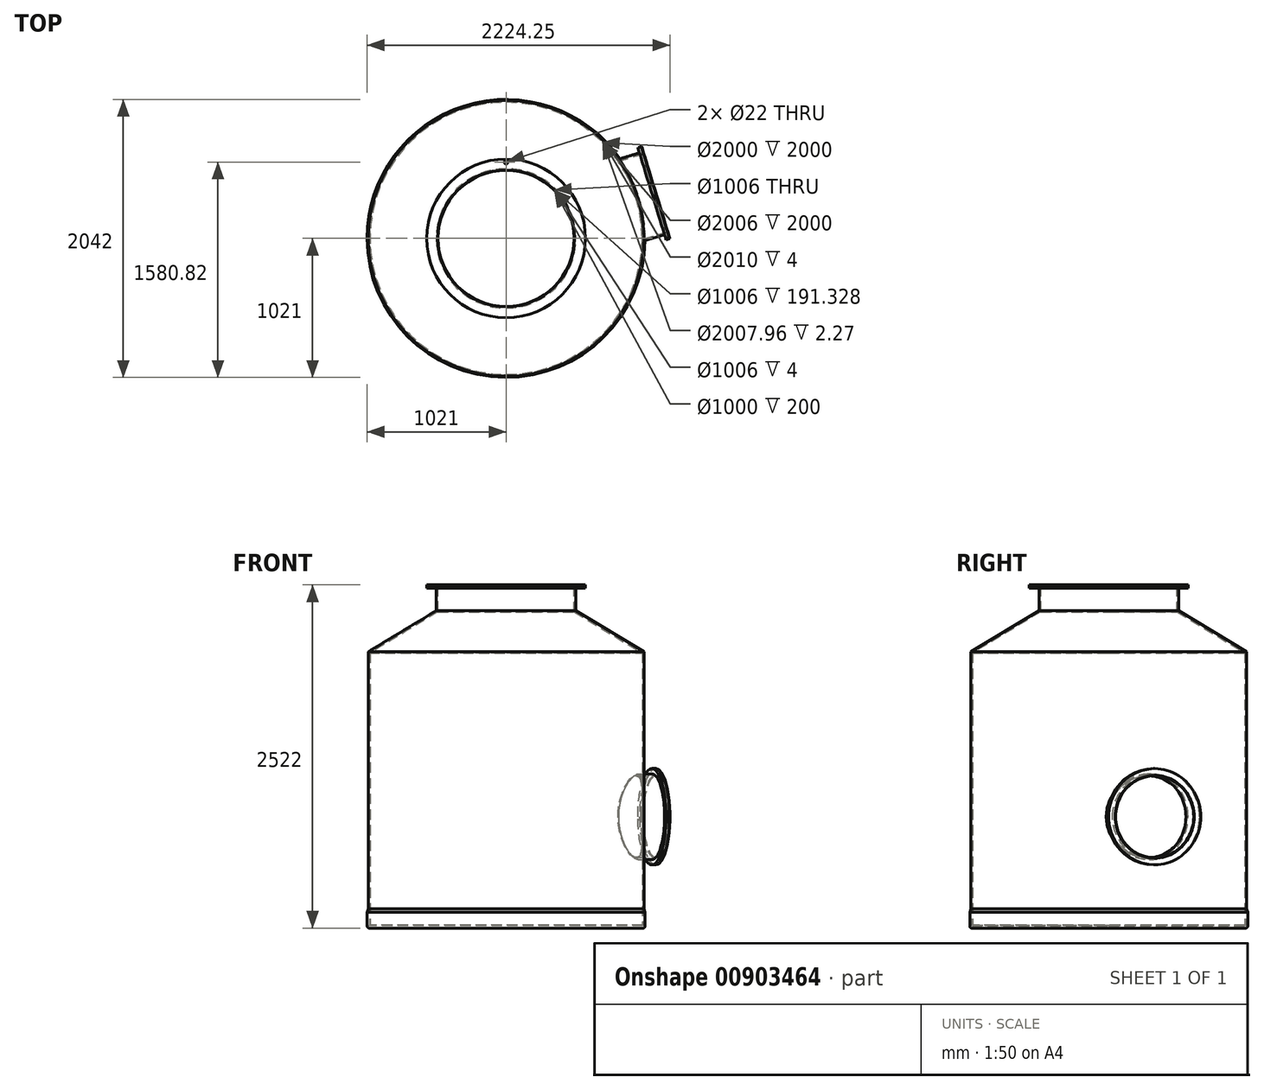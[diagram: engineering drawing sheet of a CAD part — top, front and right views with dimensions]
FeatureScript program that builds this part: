
annotation { "Feature Type Name" : "Feature", "Feature Type Description" : "" }
export const myFeature = defineFeature(function(context is Context, id is Id, definition is map)
    precondition{}
    {
        {
            var Q0;
            Q0=qCreatedBy(makeId("Top.planeOp"),FACE);
            var sketch = newSketch(context, id + "F0", { "sketchPlane" : qUnion([Q0])});
            skCircle(sketch, "E0", {"center": v(0, 0) * mm, "radius": 1005 * mm});
            skSolve(sketch);
        }
        {
            var Q0;
            Q0 = qSketchRegion(id + "F0", true);
            extrude(context, id + "F1", {"entities" : qUnion([Q0]), "depth" : 4 * mm, "offsetDistance" : 25 * mm});
        }
        {
            var Q0;
            Q0=makeQuery(id+"F1.opExtrude","CAP_FACE",FACE,{"disambiguationData":[OSD([sQuery(id+"F0.wireOp",EDGE,"E0")])],"isStart":false});
            var sketch = newSketch(context, id + "F2", { "sketchPlane" : qUnion([Q0])});
            skCircle(sketch, "E1", {"center": v(0, 0) * mm, "radius": 1000 * mm});
            skCircle(sketch, "E2.0", {"center": v(0, 0) * mm, "radius": 1003 * mm});
            skSolve(sketch);
        }
        {
            var Q0;
            Q0=makeQuery(id+"F2.imprint","IMPRINT",FACE,{"disambiguationData":[TD([[makeQuery(id+"F2.imprint","IMPRINT",EDGE,{"derivedFrom":sQuery(id+"F2.wireOp",EDGE,"E1")}),-1.0]])]});
            extrude(context, id + "F3", {"entities" : qUnion([Q0]), "depth" : 2000 * mm, "offsetDistance" : 25 * mm});
        }
        {
            var Q0;
            Q0=makeQuery(id+"F2.imprint","IMPRINT",FACE,{"disambiguationData":[TD([[makeQuery(id+"F2.imprint","IMPRINT",EDGE,{"derivedFrom":sQuery(id+"F2.wireOp",EDGE,"E1")}),1.0]])]});
            cPlane(context, id + "F4", {"entities" : qUnion([Q0]), "cplaneType" : CPlaneType.OFFSET, "offset" : 2500 * mm, "width" : 150 * mm, "height" : 150 * mm});
        }
        {
            var Q0;
            Q0=qCreatedBy(id+"F4.planeOp",FACE);
            var sketch = newSketch(context, id + "F5", { "sketchPlane" : qUnion([Q0])});
            skCircle(sketch, "E3", {"center": v(0, 0) * mm, "radius": 500 * mm});
            skCircle(sketch, "E4.0", {"center": v(0, 0) * mm, "radius": 503 * mm});
            skSolve(sketch);
        }
        {
            var Q0;
            Q0=makeQuery(id+"F5.imprint","IMPRINT",FACE,{"disambiguationData":[TD([[makeQuery(id+"F5.imprint","IMPRINT",EDGE,{"derivedFrom":sQuery(id+"F5.wireOp",EDGE,"E3")}),-1.0]])]});
            extrude(context, id + "F6", {"entities" : qUnion([Q0]), "oppositeDirection" : true, "depth" : 200 * mm, "offsetDistance" : 25 * mm});
        }
        {
            var Q0;
            Q0=makeQuery(id+"F6.opExtrude","CAP_FACE",FACE,{"disambiguationData":[OSD([sQuery(id+"F5.wireOp",EDGE,"E3"),sQuery(id+"F5.wireOp",EDGE,"E4.0")])],"isStart":true});
            var sketch = newSketch(context, id + "F7", { "sketchPlane" : qUnion([Q0])});
            skCircle(sketch, "E5.0", {"center": v(0, 0) * mm, "radius": 503 * mm});
            skCircle(sketch, "E6.0", {"center": v(0, 0) * mm, "radius": 583 * mm});
            skSolve(sketch);
        }
        {
            var Q0;
            Q0 = qSketchRegion(id + "F7", true);
            extrude(context, id + "F8", {"entities" : qUnion([Q0]), "oppositeDirection" : true, "depth" : 4 * mm, "offsetDistance" : 25 * mm});
        }
        {
            var Q0;
            Q0=makeQuery(id+"F6.opExtrude","CAP_FACE",FACE,{"disambiguationData":[OSD([sQuery(id+"F5.wireOp",EDGE,"E3"),sQuery(id+"F5.wireOp",EDGE,"E4.0")])],"isStart":false});
            var sketch = newSketch(context, id + "F9", { "sketchPlane" : qUnion([Q0])});
            skLineSegment(sketch, "E7", {"start": v(0, 0) * mm, "end": v(1061.3, 0) * mm, "construction": true});
            skCircle(sketch, "E8.0", {"center": v(0, 0) * mm, "radius": 503 * mm});
            skPoint(sketch, "E9", {"position": v(503, 0) * mm});
            skSolve(sketch);
        }
        {
            var Q0;
            Q0=makeQuery(id+"F3.opExtrude","CAP_FACE",FACE,{"disambiguationData":[OSD([sQuery(id+"F2.wireOp",EDGE,"E1"),sQuery(id+"F2.wireOp",EDGE,"E2.0")])],"isStart":false});
            var sketch = newSketch(context, id + "F10", { "sketchPlane" : qUnion([Q0])});
            skLineSegment(sketch, "E10", {"start": v(0, 0) * mm, "end": v(1069.28, 0) * mm, "construction": true});
            skCircle(sketch, "E11.0", {"center": v(0, 0) * mm, "radius": 1000 * mm});
            skPoint(sketch, "E12", {"position": v(1000, 0) * mm});
            skSolve(sketch);
        }
        {
            var Q0;
            Q0=sQuery(id+"F9.wireOp",VERTEX,"E9");
            var Q1;
            Q1=sQuery(id+"F10.wireOp",VERTEX,"E12");
            var Q2;
            Q2=qCreatedBy(makeId("Origin.pointOp"),VERTEX);
            cPlane(context, id + "F11", {"entities" : qUnion([Q0, Q1, Q2]), "cplaneType" : CPlaneType.THREE_POINT, "offset" : 25 * mm, "width" : 150 * mm, "height" : 150 * mm});
        }
        {
            var Q0;
            Q0=qCreatedBy(id+"F11.planeOp",FACE);
            var sketch = newSketch(context, id + "F12", { "sketchPlane" : qUnion([Q0])});
            skPoint(sketch, "E13.0", {"position": v(503, 2304) * mm});
            skPoint(sketch, "E14.0", {"position": v(1000, 2004) * mm});
            skLineSegment(sketch, "E15", {"start": v(503, 2304) * mm, "end": v(1000, 2004) * mm});
            skLineSegment(sketch, "E16.0", {"start": v(503, 2308.67) * mm, "end": v(1003.98, 2006.27) * mm});
            skLineSegment(sketch, "E17", {"start": v(503, 2308.67) * mm, "end": v(503, 2304) * mm});
            skLineSegment(sketch, "E18", {"start": v(1000, 2004) * mm, "end": v(1003.98, 2004) * mm});
            skLineSegment(sketch, "E19", {"start": v(1003.98, 2004) * mm, "end": v(1003.98, 2006.27) * mm});
            skSolve(sketch);
        }
        {
            var Q0;
            Q0=makeQuery(id+"F12.imprint","IMPRINT",FACE,{"disambiguationData":[TD([[makeQuery(id+"F12.imprint","IMPRINT",EDGE,{"derivedFrom":sQuery(id+"F12.wireOp",EDGE,"E15")}),1.0]])]});
            var Q1;
            Q1=sQuery(id+"F10.wireOp",EDGE,"E11.0");
            revolve(context, id + "F13", {"surfaceOperationType" : NewSurfaceOperationType.NEW, "entities" : qUnion([Q0]), "axis" : qUnion([Q1]), "revolveType" : RevolveType.FULL});
        }
        {
            var Q0;
            Q0=qCreatedBy(id+"F11.planeOp",FACE);
            var sketch = newSketch(context, id + "F14", { "sketchPlane" : qUnion([Q0])});
            skLineSegment(sketch, "E20", {"start": v(1005, 4) * mm, "end": v(1005, 0) * mm});
            skLineSegment(sketch, "E21.0", {"start": v(0, 0) * mm, "end": v(1005, 0) * mm});
            skLineSegment(sketch, "E22.0", {"start": v(1003, 4) * mm, "end": v(1005, 4) * mm});
            skLineSegment(sketch, "E23", {"start": v(1003, 2004) * mm, "end": v(1003, 4) * mm});
            skLineSegment(sketch, "E24.0", {"start": v(1003.98, 2004) * mm, "end": v(1003, 2004) * mm});
            skLineSegment(sketch, "E25", {"start": v(1003.98, 2006.27) * mm, "end": v(1003.98, 2004) * mm});
            skLineSegment(sketch, "E26", {"start": v(503, 2308.67) * mm, "end": v(1003.98, 2006.27) * mm});
            skLineSegment(sketch, "E27", {"start": v(503, 2500) * mm, "end": v(503, 2308.67) * mm});
            skLineSegment(sketch, "E28.0", {"start": v(-583, 2500) * mm, "end": v(583, 2500) * mm});
            skLineSegment(sketch, "E29", {"start": v(583, 2500) * mm, "end": v(583, 2480) * mm});
            skLineSegment(sketch, "E30.0", {"start": v(513, 2314.32) * mm, "end": v(1013, 2012.5) * mm});
            skLineSegment(sketch, "E31.trimOffspring", {"start": v(513, 2480) * mm, "end": v(513, 2314.32) * mm});
            skLineSegment(sketch, "E32.trimOffspring", {"start": v(513, 2480) * mm, "end": v(583, 2480) * mm});
            skPoint(sketch, "E33.orphan", {"position": v(-1003.98, 2004) * mm});
            skLineSegment(sketch, "E34.0", {"start": v(1013, 2012.5) * mm, "end": v(1013, 124.02) * mm});
            skPoint(sketch, "E35.orphan", {"position": v(-1005, 4) * mm});
            skLineSegment(sketch, "E36.0", {"start": v(0, -18) * mm, "end": v(1006, -18) * mm});
            skLineSegment(sketch, "E37", {"start": v(0, 0) * mm, "end": v(0, -18) * mm});
            skPoint(sketch, "E38.orphan", {"position": v(-1005, 0) * mm});
            skPoint(sketch, "E39.orphan", {"position": v(-1005, -18) * mm});
            skLineSegment(sketch, "E40.0", {"start": v(1021, 97) * mm, "end": v(1021, -3) * mm});
            skArc(sketch, "E41.filletArc", {"start": v(1006, -18) * mm, "mid": v(1016.6, -13.6) * mm, "end": v(1021, -3) * mm});
            skLineSegment(sketch, "E42", {"start": v(1021, 97) * mm, "end": v(1013, 124.02) * mm});
            skSolve(sketch);
        }
        {
            var Q0;
            Q0=makeQuery(id+"F14.imprint","IMPRINT",FACE,{"disambiguationData":[TD([[makeQuery(id+"F14.imprint","IMPRINT",EDGE,{"derivedFrom":sQuery(id+"F14.wireOp",EDGE,"E20")}),1.0]])]});
            var Q1;
            Q1=makeQuery(id+"F1.opExtrude","CAP_EDGE",EDGE,{"disambiguationData":[OSD([sQuery(id+"F0.wireOp",EDGE,"E0")])],"isStart":true});
            revolve(context, id + "F15", {"surfaceOperationType" : NewSurfaceOperationType.NEW, "entities" : qUnion([Q0]), "axis" : qUnion([Q1]), "revolveType" : RevolveType.FULL});
        }
        {
            var Q0;
            Q0=makeQuery(id+"F8.opExtrude","CAP_FACE",FACE,{"disambiguationData":[OSD([sQuery(id+"F7.wireOp",EDGE,"E5.0"),sQuery(id+"F7.wireOp",EDGE,"E6.0")])],"isStart":true});
            var sketch = newSketch(context, id + "F16", { "sketchPlane" : qUnion([Q0])});
            skCircle(sketch, "E43", {"center": v(0, 0) * mm, "radius": 559.82 * mm, "construction": true});
            skLineSegment(sketch, "E44", {"start": v(0, 0) * mm, "end": v(0, 598.8) * mm, "construction": true});
            skPoint(sketch, "E45", {"position": v(0, 559.82) * mm});
            skSolve(sketch);
        }
        {
            var Q0;
            Q0=sQuery(id+"F16.wireOp",VERTEX,"E45");
            var Q1;
            Q1=makeQuery(id+"F8.opExtrude","SWEPT_BODY",BODY,{"disambiguationData":[OSD([sQuery(id+"F7.wireOp",EDGE,"E5.0"),sQuery(id+"F7.wireOp",EDGE,"E6.0")])]});
            var Q2;
            Q2=makeQuery(id+"F15.opRevolve","SWEPT_BODY",BODY,{"disambiguationData":[OSD([sQuery(id+"F14.wireOp",EDGE,"E20"),sQuery(id+"F14.wireOp",EDGE,"E21.0"),sQuery(id+"F14.wireOp",EDGE,"E22.0"),sQuery(id+"F14.wireOp",EDGE,"E23"),sQuery(id+"F14.wireOp",EDGE,"E24.0"),sQuery(id+"F14.wireOp",EDGE,"E25"),sQuery(id+"F14.wireOp",EDGE,"E26"),sQuery(id+"F14.wireOp",EDGE,"E27"),sQuery(id+"F14.wireOp",EDGE,"E28.0"),sQuery(id+"F14.wireOp",EDGE,"E29"),sQuery(id+"F14.wireOp",EDGE,"E30.0"),sQuery(id+"F14.wireOp",EDGE,"E31.trimOffspring"),sQuery(id+"F14.wireOp",EDGE,"E32.trimOffspring"),sQuery(id+"F14.wireOp",EDGE,"E34.0"),sQuery(id+"F14.wireOp",EDGE,"E36.0"),sQuery(id+"F14.wireOp",EDGE,"E37"),sQuery(id+"F14.wireOp",EDGE,"E40.0"),sQuery(id+"F14.wireOp",EDGE,"E41.filletArc"),sQuery(id+"F14.wireOp",EDGE,"E42")])]});
            hole(context, id + "F17", {"style" : HoleStyle.C_SINK, "endStyle" : HoleEndStyle.BLIND, "holeDiameter" : 22 * mm, "cSinkDiameter" : 25 * mm, "cSinkAngle" : 90 * degree, "majorDiameter" : 5 * mm, "holeDepth" : 30 * mm, "isTappedThrough" : true, "tappedDepth" : 12 * mm, "tapClearance" : 3, "locations" : qUnion([Q0]), "scope" : qUnion([Q1, Q2]), "startStyle" : HoleStartStyle.PART});
        }
        {
            var Q0;
            Q0=qCreatedBy(makeId("Top.planeOp"),FACE);
            var sketch = newSketch(context, id + "F18", { "sketchPlane" : qUnion([Q0])});
            skLineSegment(sketch, "E46", {"start": v(0, 0) * mm, "end": v(0, 1263.36) * mm, "construction": true});
            skLineSegment(sketch, "E47", {"start": v(0, 0) * mm, "end": v(1250.42, 383.15) * mm, "construction": true});
            skCircle(sketch, "E48.0", {"center": v(0, 0) * mm, "radius": 1150 * mm, "construction": true});
            skPoint(sketch, "E49", {"position": v(1099.54, 336.92) * mm});
            skSolve(sketch);
        }
        {
            var Q0;
            Q0=sQuery(id+"F18.wireOp",VERTEX,"E49");
            var Q1;
            Q1=sQuery(id+"F18.wireOp",EDGE,"E47");
            cPlane(context, id + "F19", {"entities" : qUnion([Q0, Q1]), "cplaneType" : CPlaneType.LINE_POINT, "offset" : 25 * mm, "width" : 150 * mm, "height" : 150 * mm});
        }
        {
            var Q0;
            Q0=qCreatedBy(id+"F19.planeOp",FACE);
            var sketch = newSketch(context, id + "F20", { "sketchPlane" : qUnion([Q0])});
            skPoint(sketch, "E50", {"position": v(0, 800) * mm});
            skSolve(sketch);
        }
        {
            var Q0;
            Q0=sQuery(id+"F20.wireOp",VERTEX,"E50");
            var Q1;
            Q1=makeQuery(id+"F3.opExtrude","SWEPT_BODY",BODY,{"disambiguationData":[OSD([sQuery(id+"F2.wireOp",EDGE,"E1"),sQuery(id+"F2.wireOp",EDGE,"E2.0")])]});
            var Q2;
            Q2=makeQuery(id+"F15.opRevolve","SWEPT_BODY",BODY,{"disambiguationData":[OSD([sQuery(id+"F14.wireOp",EDGE,"E20"),sQuery(id+"F14.wireOp",EDGE,"E21.0"),sQuery(id+"F14.wireOp",EDGE,"E22.0"),sQuery(id+"F14.wireOp",EDGE,"E23"),sQuery(id+"F14.wireOp",EDGE,"E24.0"),sQuery(id+"F14.wireOp",EDGE,"E25"),sQuery(id+"F14.wireOp",EDGE,"E26"),sQuery(id+"F14.wireOp",EDGE,"E27"),sQuery(id+"F14.wireOp",EDGE,"E28.0"),sQuery(id+"F14.wireOp",EDGE,"E29"),sQuery(id+"F14.wireOp",EDGE,"E30.0"),sQuery(id+"F14.wireOp",EDGE,"E31.trimOffspring"),sQuery(id+"F14.wireOp",EDGE,"E32.trimOffspring"),sQuery(id+"F14.wireOp",EDGE,"E34.0"),sQuery(id+"F14.wireOp",EDGE,"E36.0"),sQuery(id+"F14.wireOp",EDGE,"E37"),sQuery(id+"F14.wireOp",EDGE,"E40.0"),sQuery(id+"F14.wireOp",EDGE,"E41.filletArc"),sQuery(id+"F14.wireOp",EDGE,"E42")])]});
            hole(context, id + "F21", {"style" : HoleStyle.SIMPLE, "endStyle" : HoleEndStyle.BLIND, "holeDiameter" : 608 * mm, "majorDiameter" : 5 * mm, "holeDepth" : 200 * mm, "isTappedThrough" : true, "tappedDepth" : 12 * mm, "tapClearance" : 3, "locations" : qUnion([Q0]), "scope" : qUnion([Q1, Q2]), "startStyle" : HoleStartStyle.PART});
        }
        {
            var Q0;
            Q0=qCreatedBy(id+"F19.planeOp",FACE);
            var sketch = newSketch(context, id + "F22", { "sketchPlane" : qUnion([Q0])});
            skPoint(sketch, "E51.0", {"position": v(0, 800) * mm});
            skCircle(sketch, "E52", {"center": v(0, 800) * mm, "radius": 304 * mm});
            skCircle(sketch, "E53", {"center": v(0, 800) * mm, "radius": 300 * mm});
            skSolve(sketch);
        }
        {
            var Q0;
            Q0=makeQuery(id+"F22.imprint","IMPRINT",FACE,{"disambiguationData":[TD([[makeQuery(id+"F22.imprint","IMPRINT",EDGE,{"derivedFrom":sQuery(id+"F22.wireOp",EDGE,"E52")}),1.0]])]});
            var Q1;
            Q1=makeQuery(id+"F3.opExtrude","SWEPT_FACE",FACE,{"disambiguationData":[OSD([sQuery(id+"F2.wireOp",EDGE,"E1")])]});
            extrude(context, id + "F23", {"entities" : qUnion([Q0]), "endBound" : BoundingType.UP_TO_SURFACE, "oppositeDirection" : true, "depth" : 25 * mm, "endBoundEntityFace" : qUnion([Q1]), "offsetDistance" : 25 * mm});
        }
        {
            var Q0;
            Q0=makeQuery(id+"F23.opExtrude","CAP_FACE",FACE,{"disambiguationData":[OSD([sQuery(id+"F22.wireOp",EDGE,"E52"),sQuery(id+"F22.wireOp",EDGE,"E53")])],"isStart":true});
            var sketch = newSketch(context, id + "F24", { "sketchPlane" : qUnion([Q0])});
            skCircle(sketch, "E54.0", {"center": v(0, 800) * mm, "radius": 304 * mm});
            skCircle(sketch, "E55.0", {"center": v(0, 800) * mm, "radius": 354 * mm});
            skSolve(sketch);
        }
        {
            var Q0;
            Q0=makeQuery(id+"F24.imprint","IMPRINT",FACE,{"disambiguationData":[TD([[makeQuery(id+"F24.imprint","IMPRINT",EDGE,{"derivedFrom":sQuery(id+"F24.wireOp",EDGE,"E54.0")}),-1.0]])]});
            extrude(context, id + "F25", {"entities" : qUnion([Q0]), "oppositeDirection" : true, "depth" : 4 * mm, "offsetDistance" : 25 * mm});
        }
        {
            var Q0;
            Q0=makeQuery(id+"F25.opExtrude","CAP_FACE",FACE,{"disambiguationData":[OSD([sQuery(id+"F24.wireOp",EDGE,"E54.0"),sQuery(id+"F24.wireOp",EDGE,"E55.0")])],"isStart":false});
            var sketch = newSketch(context, id + "F26", { "sketchPlane" : qUnion([Q0])});
            skCircle(sketch, "E56.0", {"center": v(0, 800) * mm, "radius": 304 * mm});
            skCircle(sketch, "E57.0", {"center": v(0, 800) * mm, "radius": 354 * mm});
            skSolve(sketch);
        }
        {
            var Q0;
            Q0=makeQuery(id+"F26.imprint","IMPRINT",FACE,{"disambiguationData":[TD([[makeQuery(id+"F26.imprint","IMPRINT",EDGE,{"derivedFrom":sQuery(id+"F26.wireOp",EDGE,"E56.0")}),1.0]])]});
            extrude(context, id + "F27", {"entities" : qUnion([Q0]), "depth" : 25 * mm, "offsetDistance" : 25 * mm});
        }
        {
            var Q0;
            Q0=makeQuery(id+"F27.opExtrude","CAP_FACE",FACE,{"disambiguationData":[OSD([sQuery(id+"F26.wireOp",EDGE,"E56.0"),sQuery(id+"F26.wireOp",EDGE,"E57.0")])],"isStart":false});
            var sketch = newSketch(context, id + "F28", { "sketchPlane" : qUnion([Q0])});
            skCircle(sketch, "E58.0", {"center": v(0, 800) * mm, "radius": 304 * mm});
            skCircle(sketch, "E59.0", {"center": v(0, 800) * mm, "radius": 314 * mm});
            skSolve(sketch);
        }
        {
            var Q0;
            Q0=makeQuery(id+"F28.imprint","IMPRINT",FACE,{"disambiguationData":[TD([[makeQuery(id+"F28.imprint","IMPRINT",EDGE,{"derivedFrom":sQuery(id+"F28.wireOp",EDGE,"E58.0")}),1.0]])]});
            extrude(context, id + "F29", {"entities" : qUnion([Q0]), "operationType" : NewBodyOperationType.ADD, "endBound" : BoundingType.UP_TO_NEXT, "depth" : 47 * mm, "offsetDistance" : 25 * mm});
        }
    });
